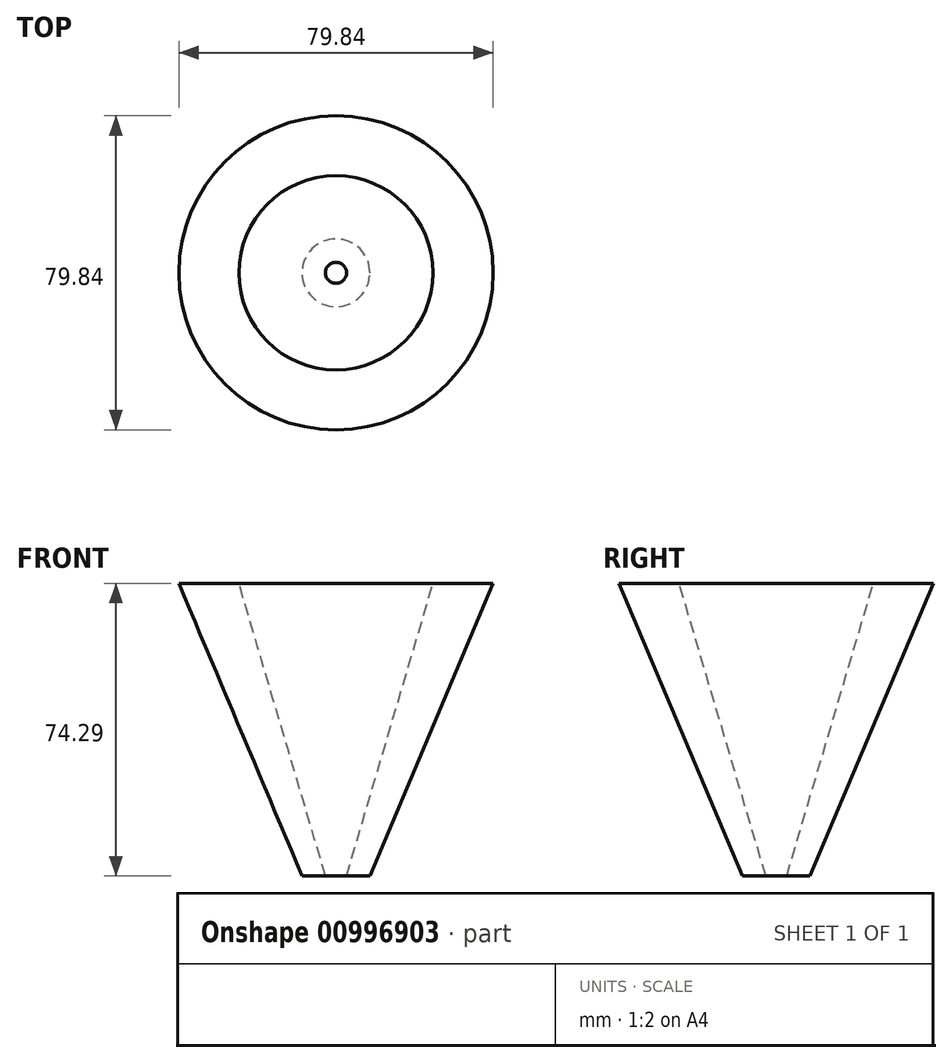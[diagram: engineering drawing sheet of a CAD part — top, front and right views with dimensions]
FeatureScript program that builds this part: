
annotation { "Feature Type Name" : "Feature", "Feature Type Description" : "" }
export const myFeature = defineFeature(function(context is Context, id is Id, definition is map)
    precondition{}
    {
        {
            var Q0;
            Q0=qCreatedBy(makeId("Front.planeOp"),FACE);
            var sketch = newSketch(context, id + "F0", { "sketchPlane" : qUnion([Q0])});
            skLineSegment(sketch, "E0", {"start": v(0, 0) * mm, "end": v(2.67, 0) * mm, "construction": true});
            skLineSegment(sketch, "E1", {"start": v(8.62, 0) * mm, "end": v(39.92, 74.3) * mm});
            skLineSegment(sketch, "E2", {"start": v(39.92, 74.3) * mm, "end": v(24.67, 74.3) * mm});
            skLineSegment(sketch, "E3", {"start": v(24.67, 74.3) * mm, "end": v(2.67, 0) * mm});
            skLineSegment(sketch, "E4", {"start": v(0, 0) * mm, "end": v(0, 35.26) * mm, "construction": true});
            skLineSegment(sketch, "E5", {"start": v(2.67, 0) * mm, "end": v(8.62, 0) * mm});
            skSolve(sketch);
        }
        {
            var Q0;
            Q0=makeQuery(id+"F0.imprint","IMPRINT",FACE,{"disambiguationData":[TD([[makeQuery(id+"F0.imprint","IMPRINT",EDGE,{"derivedFrom":sQuery(id+"F0.wireOp",EDGE,"E1")}),1.0]])]});
            var Q1;
            Q1=sQuery(id+"F0.wireOp",EDGE,"E4");
            revolve(context, id + "F1", {"surfaceOperationType" : NewSurfaceOperationType.NEW, "entities" : qUnion([Q0]), "axis" : qUnion([Q1]), "revolveType" : RevolveType.FULL});
        }
    });
